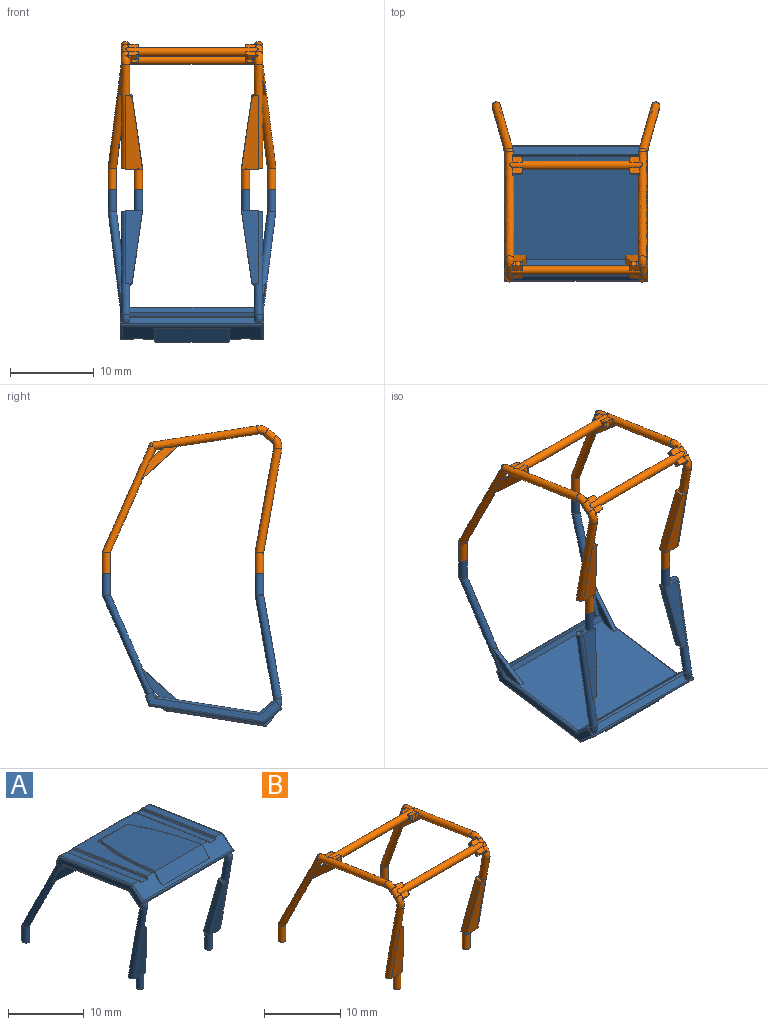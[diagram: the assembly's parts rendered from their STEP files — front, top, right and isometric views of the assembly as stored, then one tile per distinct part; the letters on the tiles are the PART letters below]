
ASSEMBLY  parts=2 mates=1
PART A: 126 faces, bbox 21.3x22.7x19.5 mm
  f0: bspline ~1.06x1.03mm, area 2.2mm2, adj f1
  f1: bspline ~12.38x3.19mm, area 25.8mm2, adj f0,f2,f14,f15,f16,f17
  f2: plane 8.76x1.55mm, normal (-1,0,0), area 0.1mm2, adj f1,f3,f14,f17
  f3: plane 8.76x2.04mm, normal (0,0.98,0.17), area 12.4mm2, adj f2,f4,f5,f10,f11,f13,f14,f17
  f4: plane 0.53x0.45mm, normal (0,0.17,-0.98), area 0.1mm2, adj f3,f5,f11
  f5: plane 8.79x2.58mm, normal (0.99,-0.02,0.14), area 8.9mm2, adj f3,f4,f6,f7,f8,f9,f10
  f6: plane 0.27x0.02mm, normal (0,0,1), area 0mm2, adj f5,f7
  f7: cylinder r=0.51mm len=0.27mm, axis (0,0,1), area 0mm2, adj f5,f6
  f8: plane 0.53x0.45mm, normal (0,0.17,-0.98), area 0.1mm2, adj f5,f9,f11
  f9: plane 8.76x2.03mm, normal (0,-0.98,-0.17), area 12.4mm2, adj f5,f8,f10,f11,f14,f15,f17
  f10: cylinder r=0.25mm len=1.04mm, axis (0,-0.98,-0.17), area 0.4mm2, adj f3,f5,f9,f14
  f11: cylinder r=0.51mm len=2.67mm, axis (0,0,1), area 8.1mm2, adj f3,f4,f8,f9,f12,f13,f17
  f12: plane 1.02x1.02mm, normal (0,0,-1), area 0.8mm2, adj f11
  f13: plane 0.24x0.01mm, normal (0,0,1), area 0mm2, adj f3,f11
  f14: plane 1.15x0.69mm, normal (0,-0.17,0.98), area 0.2mm2, adj f1,f2,f3,f9,f10,f15
  f15: plane 8.76x2.04mm, normal (-1,0,0), area 0.1mm2, adj f1,f9,f14,f16,f17
  f16: plane 1.16x1.16mm, normal (0,0,-1), area 0.6mm2, adj f1,f15,f17
  f17: plane 1.58x1.15mm, normal (0,0.17,-0.98), area 0.9mm2, adj f1,f2,f3,f9,f11,f15,f16
  f18: plane 13.56x11.3mm, normal (0,0.15,0.99), area 57.9mm2, adj f19,f91,f92,f103,f104,f105,f106,f107
  f19: bspline ~0.23x0.17mm, area 0mm2, adj f18,f20,f21,f91
  f20: bspline ~0.24x0.21mm, area 0mm2, adj f19,f21,f108
  f21: bspline ~0.41x0.41mm, area 0.1mm2, adj f19,f20,f22,f89,f90
  f22: plane 16.64x0.89mm, normal (0,0.92,0.4), area 15.2mm2, adj f21,f23,f80,f81,f82,f84,f85,f86
  f23: cylinder r=0.25mm len=1.22mm, axis (0,0.4,-0.92), area 0.4mm2, adj f22,f24,f79,f88
  f24: plane 16.01x3.52mm, normal (1,0,0), area 13.1mm2, adj f23,f25,f67,f68,f69,f70,f71,f72
  f25: plane 17.22x1mm, normal (0,0.4,-0.92), area 16mm2, adj f24,f26,f42,f43,f44,f45,f46,f47
  f26: cylinder r=0.25mm len=0.84mm, axis (0,0.4,-0.92), area 0.3mm2, adj f25,f27,f41,f42,f45,f55
  f27: cylinder r=0.25mm len=12.55mm, axis (0,0.99,-0.15), area 5mm2, adj f26,f28,f37,f55
  f28: cylinder r=0.25mm len=2.07mm, axis (0,0.77,0.64), area 0.9mm2, adj f27,f29,f36,f55
  f29: cylinder r=0.25mm len=17.15mm, axis (-1,0,0), area 6.3mm2, adj f28,f30,f33,f36,f69,f70
  f30: bspline ~1.01x1mm, area -0.1mm2, adj f29,f31,f32,f70
  f31: plane 0.04x0.04mm, normal (0,0.64,-0.77), area 0mm2, adj f30,f32,f70
  f32: bspline ~1.07x0.76mm, area 0mm2, adj f30,f31,f70
  f33: bspline ~1.02x1.01mm, area 2.7mm2, adj f29,f34,f35,f70
  f34: plane 1.26x1.25mm, normal (0,0.64,-0.77), area 0mm2, adj f33,f35,f70
  f35: bspline ~0.36x0.31mm, area 0mm2, adj f33,f34,f70
  f36: plane 16.64x1.62mm, normal (0,0.64,-0.77), area 35.2mm2, adj f28,f29,f37,f69
  f37: plane 16.64x12.26mm, normal (0,-0.15,-0.99), area 204.4mm2, adj f27,f36,f38,f39,f40,f41,f42,f44
  f38: plane 4.39x4.01mm, normal (-0.01,-0.67,-0.74), area 2.8mm2, adj f37,f42,f44,f52
  f39: plane 4.39x4.01mm, normal (0.01,-0.67,-0.74), area 2.8mm2, adj f37,f46,f48,f49
  f40: plane 0.73x0.66mm, normal (-0.01,0.67,0.74), area 0.5mm2, adj f37,f45,f46,f48,f67
  f41: plane 0.73x0.66mm, normal (0.01,0.67,0.74), area 0.5mm2, adj f26,f37,f42,f44,f45
  f42: plane 4.17x3.79mm, normal (-0.99,-0.09,0.09), area 3.9mm2, adj f25,f26,f37,f38,f41,f43,f52
  f43: plane 0.81x0.72mm, normal (0.01,0.67,0.74), area 0.2mm2, adj f25,f42,f44,f52
  f44: plane 3.99x3.62mm, normal (0.99,0.09,-0.09), area 3.6mm2, adj f25,f37,f38,f41,f43,f45,f52
  f45: plane 16.64x0.61mm, normal (0,-0.92,-0.4), area 11.1mm2, adj f25,f26,f37,f40,f41,f44,f46,f67
  f46: plane 3.99x3.62mm, normal (-0.99,0.09,-0.09), area 3.6mm2, adj f25,f37,f39,f40,f45,f47,f49
  f47: plane 0.81x0.72mm, normal (-0.01,0.67,0.74), area 0.2mm2, adj f25,f46,f48,f49
  f48: plane 4.17x3.79mm, normal (0.99,-0.09,0.09), area 3.9mm2, adj f25,f37,f39,f40,f47,f49,f67
  f49: bspline ~11.92x6.25mm, area 38.1mm2, adj f25,f39,f46,f47,f48,f50,f88
  f50: cylinder r=0.51mm len=2.54mm, axis (0,0,1), area 8.1mm2, adj f49,f51
  f51: plane 1.02x1.02mm, normal (0,0,-1), area 0.8mm2, adj f50
  f52: bspline ~11.92x6.25mm, area 38.1mm2, adj f25,f38,f42,f43,f44,f53,f88
  f53: cylinder r=0.51mm len=2.54mm, axis (0,0,1), area 8.1mm2, adj f52,f54
  f54: plane 1.02x1.02mm, normal (0,0,-1), area 0.8mm2, adj f53
  f55: plane 16.01x3.52mm, normal (-1,0,0), area 13.1mm2, adj f25,f26,f27,f28,f56,f65,f70,f87
  f56: cylinder r=0.25mm len=13.59mm, axis (0,-0.99,0.15), area 5.5mm2, adj f55,f57,f58,f65
  f57: sphere r=0.25mm, area 0mm2, adj f56,f86,f87
  f58: plane 13.56x2.11mm, normal (0,0.15,0.99), area 15.7mm2, adj f56,f59,f61,f86,f105
  f59: bspline ~0.23x0.17mm, area 0mm2, adj f58,f60,f61,f85
  f60: bspline ~0.24x0.21mm, area 0mm2, adj f59,f85,f86
  f61: cylinder r=0.13mm len=13.6mm, axis (0,-0.99,0.15), area 2.7mm2, adj f58,f59,f62,f105
  f62: cylinder r=0.13mm len=13.95mm, axis (0,0.99,-0.15), area 2.8mm2, adj f61,f63,f85,f105
  f63: plane 13.94x2.17mm, normal (0,0.15,0.99), area 14.3mm2, adj f62,f64,f84,f105
  f64: cylinder r=0.13mm len=13.95mm, axis (0,-0.99,0.15), area 2.8mm2, adj f63,f82,f105,f106
  f65: cylinder r=0.25mm len=2.33mm, axis (0,-0.77,-0.64), area 1.1mm2, adj f55,f56,f66,f105
  f66: cylinder r=0.25mm len=17.15mm, axis (-1,0,0), area 6.7mm2, adj f65,f70,f71,f105
  f67: cylinder r=0.25mm len=0.84mm, axis (0,-0.4,0.92), area 0.3mm2, adj f24,f25,f40,f45,f48,f68
  f68: cylinder r=0.25mm len=12.55mm, axis (0,-0.99,0.15), area 5mm2, adj f24,f37,f67,f69
  f69: cylinder r=0.25mm len=2.07mm, axis (0,-0.77,-0.64), area 0.9mm2, adj f24,f29,f36,f68
  f70: plane 18.35x1.9mm, normal (0,-0.77,-0.64), area 13.9mm2, adj f24,f29,f30,f31,f32,f33,f34,f35
  f71: cylinder r=0.25mm len=2.33mm, axis (0,0.77,0.64), area 1.1mm2, adj f24,f66,f72,f105
  f72: cylinder r=0.25mm len=13.59mm, axis (0,0.99,-0.15), area 5.5mm2, adj f24,f71,f73,f79
  f73: plane 13.56x2.11mm, normal (0,0.15,0.99), area 15.7mm2, adj f72,f74,f77,f80,f105
  f74: cylinder r=0.13mm len=13.6mm, axis (0,-0.99,0.15), area 2.7mm2, adj f73,f75,f77,f105
  f75: cylinder r=0.13mm len=13.95mm, axis (0,-0.99,0.15), area 2.8mm2, adj f74,f76,f81,f105
  f76: plane 13.94x2.17mm, normal (0,0.15,0.99), area 14.3mm2, adj f75,f89,f90,f105
  f77: bspline ~0.23x0.17mm, area 0mm2, adj f73,f74,f78,f81
  f78: bspline ~0.24x0.21mm, area 0mm2, adj f77,f80,f81
  f79: sphere r=0.25mm, area 0mm2, adj f23,f72,f80
  f80: cylinder r=0.25mm len=1.13mm, axis (-1,0,0), area 0.3mm2, adj f22,f73,f78,f79
  f81: bspline ~0.45x0.43mm, area 0.1mm2, adj f22,f75,f77,f78,f89
  f82: bspline ~0.45x0.43mm, area 0.1mm2, adj f22,f64,f83,f84,f107
  f83: bspline ~0.24x0.21mm, area 0mm2, adj f82,f107,f108
  f84: cylinder r=0.25mm len=1.02mm, axis (-1,0,0), area 0.3mm2, adj f22,f63,f82,f85
  f85: bspline ~0.41x0.41mm, area 0.1mm2, adj f22,f59,f60,f62,f84
  f86: cylinder r=0.25mm len=1.13mm, axis (-1,0,0), area 0.3mm2, adj f22,f57,f58,f60
  f87: cylinder r=0.25mm len=1.22mm, axis (0,-0.4,0.92), area 0.4mm2, adj f22,f55,f57,f88
  f88: cylinder r=0.25mm len=17.15mm, axis (-1,0,0), area 6.7mm2, adj f22,f23,f25,f49,f52,f87
  f89: cylinder r=0.25mm len=1.02mm, axis (-1,0,0), area 0.3mm2, adj f21,f22,f76,f81
  f90: cylinder r=0.13mm len=13.95mm, axis (0,0.99,-0.15), area 2.8mm2, adj f21,f76,f91,f105
  f91: cylinder r=0.13mm len=13.6mm, axis (0,0.99,-0.15), area 2.7mm2, adj f18,f19,f90,f105
  f92: torus R=42.74mm, axis (0,-0.15,-0.99), area 2.5mm2, adj f18,f93,f101,f102,f103,f105
  f93: plane 5.23x0.28mm, normal (0,0.69,0.72), area 1.9mm2, adj f92,f94,f100,f101,f103,f104
  f94: cylinder r=0.13mm len=5.17mm, axis (-1,0,0), area 0.4mm2, adj f93,f95,f100,f101
  f95: plane 12.05x8.64mm, normal (0,0.15,0.99), area 90.9mm2, adj f94,f96,f100,f101
  f96: plane 8.92x1.65mm, normal (0,-0.77,0.64), area 18.8mm2, adj f95,f97,f98,f99,f102,f105
  f97: cylinder r=0.13mm len=0.14mm, axis (0,-0.99,0.15), area 0mm2, adj f96,f101,f102
  f98: plane 1.69x1.51mm, normal (-1,0,0), area 0.4mm2, adj f96,f99,f104,f105
  f99: cylinder r=0.13mm len=0.14mm, axis (0,-0.99,0.15), area 0mm2, adj f96,f98,f100
  f100: torus R=42.49mm, axis (0,-0.15,-0.99), area 2.5mm2, adj f93,f94,f95,f99,f104
  f101: torus R=42.49mm, axis (0,-0.15,-0.99), area 2.5mm2, adj f92,f93,f94,f95,f97
  f102: plane 1.69x1.51mm, normal (1,0,0), area 0.4mm2, adj f92,f96,f97,f105
  f103: cylinder r=0.13mm len=5.32mm, axis (1,0,0), area 0.4mm2, adj f18,f92,f93,f104
  f104: torus R=42.74mm, axis (0,-0.15,-0.99), area 2.5mm2, adj f18,f93,f98,f100,f103,f105
  f105: plane 16.68x2.13mm, normal (0,-0.64,0.77), area 23.6mm2, adj f18,f58,f61,f62,f63,f64,f65,f66
  f106: cylinder r=0.13mm len=13.6mm, axis (0,0.99,-0.15), area 2.7mm2, adj f18,f64,f105,f107
  f107: bspline ~0.23x0.17mm, area 0mm2, adj f18,f82,f83,f106
  f108: cylinder r=0.25mm len=11.27mm, axis (-1,0,0), area 2.8mm2, adj f18,f20,f22,f83
  f109: bspline ~12.38x3.19mm, area 25.8mm2, adj f110,f122,f123,f124,f125
  f110: plane 1.58x1.15mm, normal (0,0.17,-0.98), area 0.9mm2, adj f109,f111,f120,f121,f122,f124,f125
  f111: cylinder r=0.51mm len=2.67mm, axis (0,0,1), area 8.1mm2, adj f110,f112,f113,f118,f119,f120,f121
  f112: plane 1.02x1.02mm, normal (0,0,-1), area 0.8mm2, adj f111
  f113: plane 0.53x0.45mm, normal (0,0.17,-0.98), area 0.1mm2, adj f111,f114,f120
  f114: plane 8.79x2.58mm, normal (-0.99,-0.02,0.14), area 8.9mm2, adj f113,f115,f116,f117,f119,f120,f121
  f115: cylinder r=0.25mm len=1.04mm, axis (0,-0.98,-0.17), area 0.4mm2, adj f114,f120,f121,f123
  f116: cylinder r=0.51mm len=0.27mm, axis (0,0,1), area 0mm2, adj f114,f117
  f117: plane 0.27x0.02mm, normal (0,0,1), area 0mm2, adj f114,f116
  f118: plane 0.24x0.01mm, normal (0,0,1), area 0mm2, adj f111,f121
  f119: plane 0.53x0.45mm, normal (0,0.17,-0.98), area 0.1mm2, adj f111,f114,f121
  f120: plane 8.76x2.03mm, normal (0,-0.98,-0.17), area 12.4mm2, adj f110,f111,f113,f114,f115,f123,f124
  f121: plane 8.76x2.04mm, normal (0,0.98,0.17), area 12.4mm2, adj f110,f111,f114,f115,f118,f119,f122,f123
  f122: plane 8.76x1.55mm, normal (1,0,0), area 0.1mm2, adj f109,f110,f121,f123
  f123: plane 1.15x0.69mm, normal (0,-0.17,0.98), area 0.2mm2, adj f109,f115,f120,f121,f122,f124
  f124: plane 8.76x2.04mm, normal (1,0,0), area 0.1mm2, adj f109,f110,f120,f123,f125
  f125: plane 1.16x1.16mm, normal (0,0,-1), area 0.6mm2, adj f109,f110,f124
PART B: 118 faces, bbox 20.2x21.6x17.9 mm
  f0: bspline ~12.82x2.91mm, area 0mm2, adj f11,f13,f115
  f1: bspline ~12.82x2.9mm, area 36.5mm2, adj f8,f9,f10,f13,f15,f16,f23,f24
  f2: bspline ~2.55x1.96mm, area 2.5mm2, adj f3,f4,f5,f6,f14,f15,f55,f112
  f3: plane 1.58x0.73mm, normal (0,-0.64,0.77), area 0.8mm2, adj f2,f7,f14,f42,f49,f53,f112
  f4: plane 1.38x0.73mm, normal (0,-0.64,0.77), area 0.8mm2, adj f2,f15,f41,f43,f50,f54,f112
  f5: plane 1.23x0.79mm, normal (0,0.64,-0.77), area 0.8mm2, adj f2,f15,f41,f43,f50,f54,f112
  f6: plane 1.21x0.76mm, normal (0,0.64,-0.77), area 0.8mm2, adj f2,f7,f14,f42,f49,f53,f112
  f7: plane 0.86x0.82mm, normal (1,0,0), area 0.2mm2, adj f3,f6,f53,f112
  f8: plane 1.24x0.97mm, normal (0,0.15,0.99), area 0.8mm2, adj f1,f12,f45,f48,f51,f115
  f9: plane 1.24x0.96mm, normal (0,0.15,0.99), area 0.8mm2, adj f1,f44,f46,f47,f52,f115
  f10: plane 1.24x0.96mm, normal (0,-0.15,-0.99), area 0.8mm2, adj f1,f44,f46,f47,f52,f115
  f11: plane 1.21x0.84mm, normal (0,-0.15,-0.99), area 0.8mm2, adj f0,f12,f13,f45,f48,f51,f115
  f12: plane 0.82x0.55mm, normal (1,0,0), area 0.2mm2, adj f8,f11,f51,f115
  f13: plane 4.51x4.1mm, normal (0.99,0.09,-0.09), area 4.1mm2, adj f0,f1,f11,f16,f38,f39,f48,f115
  f14: bspline ~1.63x1.2mm, area 3.6mm2, adj f2,f3,f6,f22,f49
  f15: bspline ~1.43x1.23mm, area 2.9mm2, adj f1,f2,f4,f5,f50
  f16: bspline ~12.7x6.6mm, area 40.7mm2, adj f1,f13,f23,f24,f25,f38,f39,f40
  f17: plane 1.58x1.15mm, normal (0,0.17,-0.98), area 0.9mm2, adj f20,f21,f22,f28,f29,f32,f35
  f18: plane 0.53x0.45mm, normal (0,0.17,-0.98), area 0.1mm2, adj f19,f32,f35
  f19: plane 8.79x2.58mm, normal (0.99,-0.02,0.14), area 8.9mm2, adj f18,f20,f27,f31,f32,f36,f37
  f20: plane 8.76x2.04mm, normal (0,0.98,0.17), area 12.4mm2, adj f17,f19,f27,f29,f30,f31,f33,f35
  f21: plane 1.16x1.16mm, normal (0,0,-1), area 0.6mm2, adj f17,f22,f28
  f22: bspline ~12.38x3.19mm, area 25.8mm2, adj f14,f17,f21,f28,f29,f30
  f23: sphere r=0.51mm, area 0mm2, adj f1,f16
  f24: sphere r=0.51mm, area 0.6mm2, adj f1,f16
  f25: cylinder r=0.51mm len=2.54mm, axis (0,0,1), area 8.1mm2, adj f16,f26
  f26: plane 1.02x1.02mm, normal (0,0,-1), area 0.8mm2, adj f25
  f27: plane 0.53x0.45mm, normal (0,0.17,-0.98), area 0.1mm2, adj f19,f20,f35
  f28: plane 8.76x2.04mm, normal (-1,0,0), area 0.1mm2, adj f17,f21,f22,f30,f32
  f29: plane 8.76x1.55mm, normal (-1,0,0), area 0.1mm2, adj f17,f20,f22,f30
  f30: plane 1.15x0.69mm, normal (0,-0.17,0.98), area 0.2mm2, adj f20,f22,f28,f29,f31,f32
  f31: cylinder r=0.25mm len=1.04mm, axis (0,-0.98,-0.17), area 0.4mm2, adj f19,f20,f30,f32
  f32: plane 8.76x2.03mm, normal (0,-0.98,-0.17), area 12.4mm2, adj f17,f18,f19,f28,f30,f31,f35
  f33: plane 0.24x0.01mm, normal (0,0,1), area 0mm2, adj f20,f35
  f34: plane 1.02x1.02mm, normal (0,0,-1), area 0.8mm2, adj f35
  f35: cylinder r=0.51mm len=2.67mm, axis (0,0,1), area 8.1mm2, adj f17,f18,f20,f27,f32,f33,f34
  f36: plane 0.27x0.02mm, normal (0,0,1), area 0mm2, adj f19,f37
  f37: cylinder r=0.51mm len=0.27mm, axis (0,0,1), area 0mm2, adj f19,f36
  f38: plane 1.55x1.41mm, normal (0.01,0.67,0.74), area 0.9mm2, adj f1,f13,f16,f40
  f39: plane 4.68x4.25mm, normal (-0.01,-0.67,-0.74), area 2.9mm2, adj f1,f13,f16,f40
  f40: plane 4.38x3.98mm, normal (-0.99,-0.09,0.09), area 4.2mm2, adj f1,f16,f38,f39
  f41: plane 0.68x0.59mm, normal (0,0.77,0.64), area 0.4mm2, adj f4,f5,f50,f54
  f42: plane 0.73x0.58mm, normal (0,-0.77,-0.64), area 0.4mm2, adj f3,f6,f49,f53
  f43: plane 0.86x0.82mm, normal (1,0,0), area 0.2mm2, adj f4,f5,f54,f112
  f44: plane 0.75x0.61mm, normal (0,0.99,-0.15), area 0.4mm2, adj f9,f10,f47,f52
  f45: plane 0.75x0.61mm, normal (0,-0.99,0.15), area 0.4mm2, adj f8,f11,f48,f51
  f46: plane 0.82x0.53mm, normal (1,0,0), area 0.2mm2, adj f9,f10,f52,f115
  f47: bspline ~1.26x0.5mm, area 0.3mm2, adj f1,f9,f10,f44
  f48: bspline ~1.26x0.5mm, area 0.3mm2, adj f1,f8,f11,f13,f45
  f49: bspline ~1.03x0.76mm, area 0.3mm2, adj f3,f6,f14,f42
  f50: bspline ~1.03x0.99mm, area 0.3mm2, adj f4,f5,f15,f41
  f51: cylinder r=0.25mm len=0.79mm, axis (0,0.15,0.99), area 0.3mm2, adj f8,f11,f12,f45
  f52: cylinder r=0.25mm len=0.79mm, axis (0,-0.15,-0.99), area 0.3mm2, adj f9,f10,f44,f46
  f53: cylinder r=0.25mm len=0.75mm, axis (0,-0.64,0.77), area 0.3mm2, adj f3,f6,f7,f42
  f54: cylinder r=0.25mm len=0.75mm, axis (0,0.64,-0.77), area 0.3mm2, adj f4,f5,f41,f43
  f55: plane 0.14x0.11mm, normal (-1,0,0), area 0mm2, adj f2,f112
  f56: bspline ~12.82x2.9mm, area 36.5mm2, adj f58,f59,f60,f69,f71,f72,f79,f80
  f57: bspline ~12.82x2.91mm, area 0mm2, adj f61,f69,f115
  f58: plane 1.24x0.97mm, normal (0,0.15,0.99), area 0.8mm2, adj f56,f62,f101,f104,f107,f115
  f59: plane 1.24x0.96mm, normal (0,0.15,0.99), area 0.8mm2, adj f56,f100,f102,f103,f108,f115
  f60: plane 1.24x0.96mm, normal (0,-0.15,-0.99), area 0.8mm2, adj f56,f100,f102,f103,f108,f115
  f61: plane 1.21x0.84mm, normal (0,-0.15,-0.99), area 0.8mm2, adj f57,f62,f69,f101,f104,f107,f115
  f62: plane 0.82x0.55mm, normal (-1,0,0), area 0.2mm2, adj f58,f61,f107,f115
  f63: bspline ~2.55x1.96mm, area 2.5mm2, adj f64,f65,f66,f67,f70,f71,f111,f112
  f64: plane 1.58x0.73mm, normal (0,-0.64,0.77), area 0.8mm2, adj f63,f68,f70,f98,f105,f109,f112
  f65: plane 1.38x0.73mm, normal (0,-0.64,0.77), area 0.8mm2, adj f63,f71,f97,f99,f106,f110,f112
  f66: plane 1.23x0.79mm, normal (0,0.64,-0.77), area 0.8mm2, adj f63,f71,f97,f99,f106,f110,f112
  f67: plane 1.21x0.76mm, normal (0,0.64,-0.77), area 0.8mm2, adj f63,f68,f70,f98,f105,f109,f112
  f68: plane 0.86x0.82mm, normal (-1,0,0), area 0.2mm2, adj f64,f67,f109,f112
  f69: plane 4.51x4.1mm, normal (-0.99,0.09,-0.09), area 4.1mm2, adj f56,f57,f61,f72,f94,f95,f104,f115
  f70: bspline ~1.63x1.2mm, area 3.6mm2, adj f63,f64,f67,f78,f105
  f71: bspline ~1.43x1.23mm, area 2.9mm2, adj f56,f63,f65,f66,f106
  f72: bspline ~12.7x6.6mm, area 40.7mm2, adj f56,f69,f79,f80,f81,f94,f95,f96
  f73: plane 1.58x1.15mm, normal (0,0.17,-0.98), area 0.9mm2, adj f76,f77,f78,f84,f85,f88,f91
  f74: plane 0.53x0.45mm, normal (0,0.17,-0.98), area 0.1mm2, adj f75,f88,f91
  f75: plane 8.79x2.58mm, normal (-0.99,-0.02,0.14), area 8.9mm2, adj f74,f76,f83,f87,f88,f92,f93
  f76: plane 8.76x2.04mm, normal (0,0.98,0.17), area 12.4mm2, adj f73,f75,f83,f85,f86,f87,f89,f91
  f77: plane 1.16x1.16mm, normal (0,0,-1), area 0.6mm2, adj f73,f78,f84
  f78: bspline ~12.38x3.19mm, area 25.8mm2, adj f70,f73,f77,f84,f85,f86
  f79: sphere r=0.51mm, area 0mm2, adj f56,f72
  f80: sphere r=0.51mm, area 0.6mm2, adj f56,f72
  f81: cylinder r=0.51mm len=2.54mm, axis (0,0,1), area 8.1mm2, adj f72,f82
  f82: plane 1.02x1.02mm, normal (0,0,-1), area 0.8mm2, adj f81
  f83: plane 0.53x0.45mm, normal (0,0.17,-0.98), area 0.1mm2, adj f75,f76,f91
  f84: plane 8.76x2.04mm, normal (1,0,0), area 0.1mm2, adj f73,f77,f78,f86,f88
  f85: plane 8.76x1.55mm, normal (1,0,0), area 0.1mm2, adj f73,f76,f78,f86
  f86: plane 1.15x0.69mm, normal (0,-0.17,0.98), area 0.2mm2, adj f76,f78,f84,f85,f87,f88
  f87: cylinder r=0.25mm len=1.04mm, axis (0,-0.98,-0.17), area 0.4mm2, adj f75,f76,f86,f88
  f88: plane 8.76x2.03mm, normal (0,-0.98,-0.17), area 12.4mm2, adj f73,f74,f75,f84,f86,f87,f91
  f89: plane 0.24x0.01mm, normal (0,0,1), area 0mm2, adj f76,f91
  f90: plane 1.02x1.02mm, normal (0,0,-1), area 0.8mm2, adj f91
  f91: cylinder r=0.51mm len=2.67mm, axis (0,0,1), area 8.1mm2, adj f73,f74,f76,f83,f88,f89,f90
  f92: plane 0.27x0.02mm, normal (0,0,1), area 0mm2, adj f75,f93
  f93: cylinder r=0.51mm len=0.27mm, axis (0,0,1), area 0mm2, adj f75,f92
  f94: plane 1.55x1.41mm, normal (-0.01,0.67,0.74), area 0.9mm2, adj f56,f69,f72,f96
  f95: plane 4.68x4.25mm, normal (0.01,-0.67,-0.74), area 2.9mm2, adj f56,f69,f72,f96
  f96: plane 4.38x3.98mm, normal (0.99,-0.09,0.09), area 4.2mm2, adj f56,f72,f94,f95
  f97: plane 0.68x0.59mm, normal (0,0.77,0.64), area 0.4mm2, adj f65,f66,f106,f110
  f98: plane 0.73x0.58mm, normal (0,-0.77,-0.64), area 0.4mm2, adj f64,f67,f105,f109
  f99: plane 0.86x0.82mm, normal (-1,0,0), area 0.2mm2, adj f65,f66,f110,f112
  f100: plane 0.75x0.61mm, normal (0,0.99,-0.15), area 0.4mm2, adj f59,f60,f103,f108
  f101: plane 0.75x0.61mm, normal (0,-0.99,0.15), area 0.4mm2, adj f58,f61,f104,f107
  f102: plane 0.82x0.53mm, normal (-1,0,0), area 0.2mm2, adj f59,f60,f108,f115
  f103: bspline ~1.26x0.5mm, area 0.3mm2, adj f56,f59,f60,f100
  f104: bspline ~1.26x0.5mm, area 0.3mm2, adj f56,f58,f61,f69,f101
  f105: bspline ~1.03x0.76mm, area 0.3mm2, adj f64,f67,f70,f98
  f106: bspline ~1.03x0.99mm, area 0.3mm2, adj f65,f66,f71,f97
  f107: cylinder r=0.25mm len=0.79mm, axis (0,0.15,0.99), area 0.3mm2, adj f58,f61,f62,f101
  f108: cylinder r=0.25mm len=0.79mm, axis (0,-0.15,-0.99), area 0.3mm2, adj f59,f60,f100,f102
  f109: cylinder r=0.25mm len=0.75mm, axis (0,-0.64,0.77), area 0.3mm2, adj f64,f67,f68,f98
  f110: cylinder r=0.25mm len=0.75mm, axis (0,0.64,-0.77), area 0.3mm2, adj f65,f66,f97,f99
  f111: plane 0.14x0.11mm, normal (1,0,0), area 0mm2, adj f63,f112
  f112: cylinder r=0.51mm len=15.88mm, axis (-1,0,0), area 45.1mm2, adj f2,f3,f4,f5,f6,f7,f43,f55
  f113: plane 0.14x0.11mm, normal (1,0,0), area 0mm2, adj f63,f112
  f114: plane 0.14x0.11mm, normal (-1,0,0), area 0mm2, adj f2,f112
  f115: cylinder r=0.51mm len=15.88mm, axis (-1,0,0), area 44.9mm2, adj f0,f1,f8,f9,f10,f11,f12,f13
  f116: plane 0.18x0.03mm, normal (1,0,0), area 0mm2, adj f56,f115
  f117: plane 0.18x0.03mm, normal (-1,0,0), area 0mm2, adj f1,f115
PLACE A rot(axis=(0,1,0),180deg) t=(7.04,-2.89,-2.97)mm
PLACE B t=(-8.83,-2.89,2.11)mm fixed
MATE planar A.f111 <-> B.f35  axis (0,0,1) through (-7.31,-2.89,-0.43)mm
